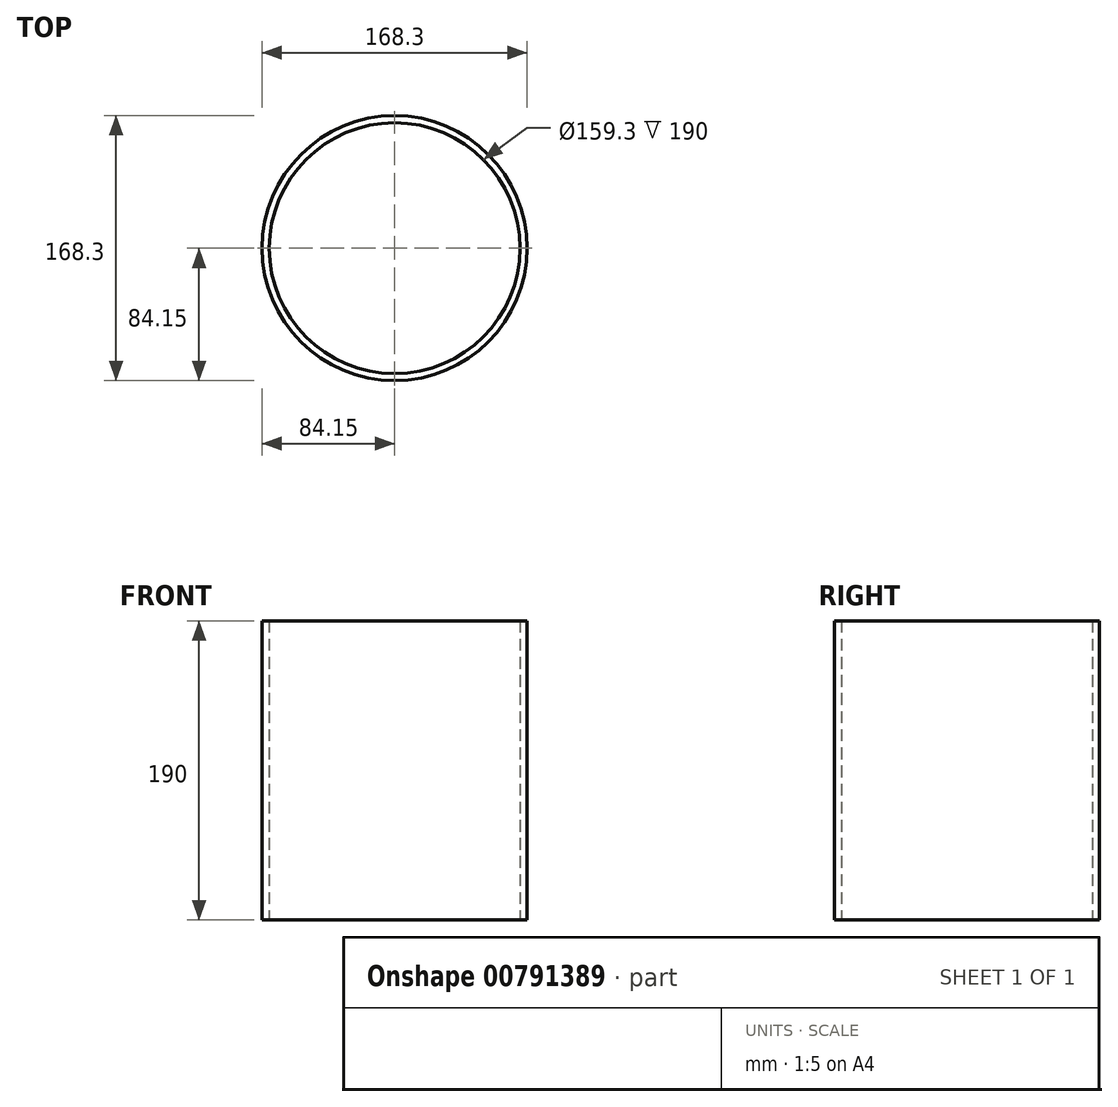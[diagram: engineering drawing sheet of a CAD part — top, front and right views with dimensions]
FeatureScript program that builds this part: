
annotation { "Feature Type Name" : "Feature", "Feature Type Description" : "" }
export const myFeature = defineFeature(function(context is Context, id is Id, definition is map)
    precondition{}
    {
        {
            var Q0;
            Q0=qCreatedBy(makeId("Top.planeOp"),FACE);
            var sketch = newSketch(context, id + "F0", { "sketchPlane" : qUnion([Q0])});
            skCircle(sketch, "E0", {"center": v(0, 0) * mm, "radius": 84.15 * mm});
            skCircle(sketch, "E1", {"center": v(0, 0) * mm, "radius": 79.65 * mm});
            skSolve(sketch);
        }
        {
            var Q0;
            Q0 = qSketchRegion(id + "F0", true);
            extrude(context, id + "F1", {"entities" : qUnion([Q0]), "depth" : 190 * mm, "offsetDistance" : 25 * mm});
        }
    });
